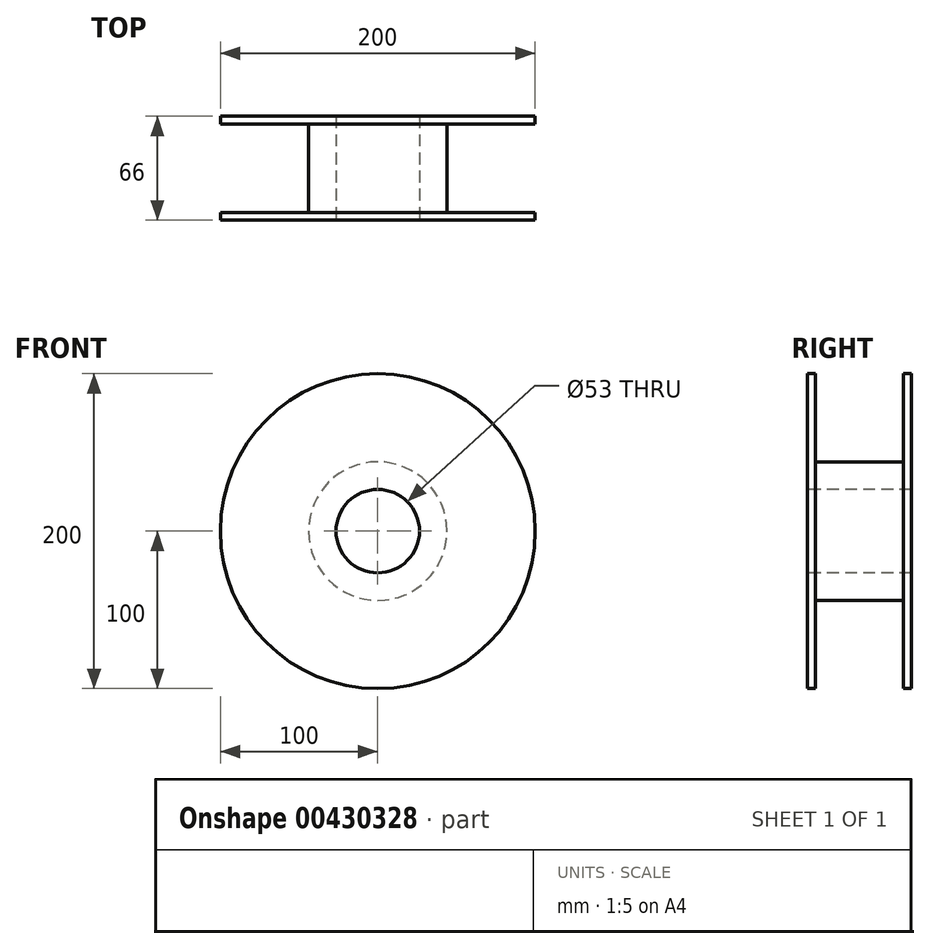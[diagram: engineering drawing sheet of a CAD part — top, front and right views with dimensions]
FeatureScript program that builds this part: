
annotation { "Feature Type Name" : "Feature", "Feature Type Description" : "" }
export const myFeature = defineFeature(function(context is Context, id is Id, definition is map)
    precondition{}
    {
        {
            var Q0;
            Q0=qCreatedBy(makeId("Right.planeOp"),FACE);
            var sketch = newSketch(context, id + "F0", { "sketchPlane" : qUnion([Q0])});
            skLineSegment(sketch, "E0", {"start": v(-33, 26.5) * mm, "end": v(-33, 100) * mm});
            skLineSegment(sketch, "E1", {"start": v(-33, 100) * mm, "end": v(-28, 100) * mm});
            skLineSegment(sketch, "E2", {"start": v(-28, 100) * mm, "end": v(-28, 44) * mm});
            skLineSegment(sketch, "E3", {"start": v(-28, 44) * mm, "end": v(28, 44) * mm});
            skLineSegment(sketch, "E4", {"start": v(28, 44) * mm, "end": v(28, 100) * mm});
            skLineSegment(sketch, "E5", {"start": v(28, 100) * mm, "end": v(33, 100) * mm});
            skLineSegment(sketch, "E6", {"start": v(33, 100) * mm, "end": v(33, 26.5) * mm});
            skLineSegment(sketch, "E7", {"start": v(33, 26.5) * mm, "end": v(-33, 26.5) * mm});
            skLineSegment(sketch, "E8", {"start": v(-33, 0) * mm, "end": v(33, 0) * mm, "construction": true});
            skSolve(sketch);
        }
        {
            var Q0;
            Q0 = qSketchRegion(id + "F0", true);
            var Q1;
            Q1=sQuery(id+"F0.wireOp",EDGE,"E8");
            revolve(context, id + "F1", {"entities" : qUnion([Q0]), "axis" : qUnion([Q1]), "revolveType" : RevolveType.FULL});
        }
    });
